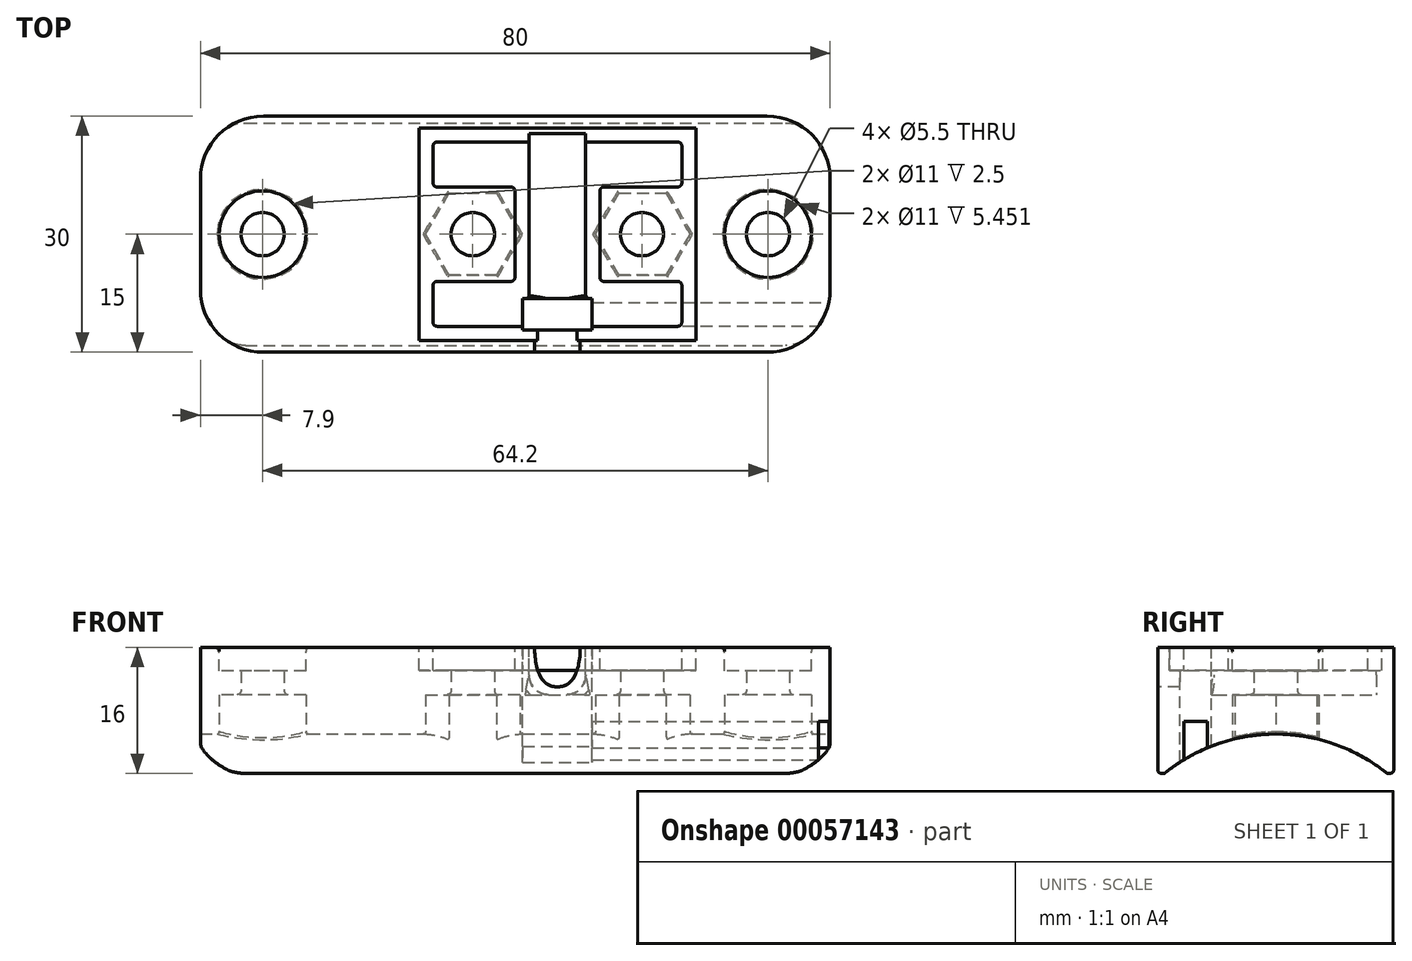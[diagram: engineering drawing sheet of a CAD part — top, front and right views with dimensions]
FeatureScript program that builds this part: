
annotation { "Feature Type Name" : "Feature", "Feature Type Description" : "" }
export const myFeature = defineFeature(function(context is Context, id is Id, definition is map)
    precondition{}
    {
        {
            var Q0;
            Q0=qCreatedBy(makeId("Top.planeOp"),FACE);
            var sketch = newSketch(context, id + "F0", { "sketchPlane" : qUnion([Q0])});
            skLineSegment(sketch, "E0.top", {"start": v(0, -15) * mm, "end": v(32, -15) * mm});
            skLineSegment(sketch, "E0.right", {"start": v(40, 7) * mm, "end": v(40, -7) * mm});
            skLineSegment(sketch, "E1", {"start": v(32, 15) * mm, "end": v(0, 15) * mm});
            skLineSegment(sketch, "E2.MirrorCS", {"start": v(0, -15) * mm, "end": v(-32, -15) * mm});
            skLineSegment(sketch, "E3.MirrorCS", {"start": v(-32, 15) * mm, "end": v(0, 15) * mm});
            skLineSegment(sketch, "E4.MirrorCS", {"start": v(-40, 7) * mm, "end": v(-40, -7) * mm});
            skCircle(sketch, "E5", {"center": v(-5.4, 0) * mm, "radius": 2.75 * mm});
            skCircle(sketch, "E6", {"center": v(16.1, 0) * mm, "radius": 2.75 * mm});
            skLineSegment(sketch, "E7", {"start": v(-5.4, 0) * mm, "end": v(16.1, 0) * mm, "construction": true});
            skLineSegment(sketch, "E8", {"start": v(16.1, 0) * mm, "end": v(40, 0) * mm, "construction": true});
            skLineSegment(sketch, "E9", {"start": v(0, 15) * mm, "end": v(0, -15) * mm, "construction": true});
            skLineSegment(sketch, "E10", {"start": v(-40, 0) * mm, "end": v(40, 0) * mm, "construction": true});
            skCircle(sketch, "E11", {"center": v(32.1, 0) * mm, "radius": 2.75 * mm});
            skCircle(sketch, "E12", {"center": v(-32.1, 0) * mm, "radius": 2.75 * mm});
            skLineSegment(sketch, "E13", {"start": v(-32.1, 0) * mm, "end": v(-40, 0) * mm, "construction": true});
            skLineSegment(sketch, "E14", {"start": v(-32.1, 0) * mm, "end": v(32.1, 0) * mm, "construction": true});
            skLineSegment(sketch, "E15", {"start": v(16.1, 0) * mm, "end": v(32.1, 0) * mm, "construction": true});
            skPoint(sketch, "E16.visualSharp", {"position": v(-40, 15) * mm});
            skArc(sketch, "E16.filletArc", {"start": v(-32, 15) * mm, "mid": v(-37.66, 12.66) * mm, "end": v(-40, 7) * mm});
            skPoint(sketch, "E17.visualSharp", {"position": v(-40, -15) * mm});
            skArc(sketch, "E17.filletArc", {"start": v(-40, -7) * mm, "mid": v(-37.66, -12.66) * mm, "end": v(-32, -15) * mm});
            skPoint(sketch, "E18.visualSharp", {"position": v(40, -15) * mm});
            skArc(sketch, "E18.filletArc", {"start": v(32, -15) * mm, "mid": v(37.66, -12.66) * mm, "end": v(40, -7) * mm});
            skPoint(sketch, "E19.visualSharp", {"position": v(40, 15) * mm});
            skArc(sketch, "E19.filletArc", {"start": v(40, 7) * mm, "mid": v(37.66, 12.66) * mm, "end": v(32, 15) * mm});
            skSolve(sketch);
        }
        {
            var Q0;
            Q0=makeQuery(id+"F0.imprint","IMPRINT",FACE,{"disambiguationData":[TD([[makeQuery(id+"F0.imprint","IMPRINT",EDGE,{"derivedFrom":sQuery(id+"F0.wireOp",EDGE,"E0.top")}),1.0]])]});
            extrude(context, id + "F1", {"entities" : qUnion([Q0]), "depth" : 14 * mm});
        }
        {
            var Q0;
            Q0=qCreatedBy(makeId("Right.planeOp"),FACE);
            var sketch = newSketch(context, id + "F2", { "sketchPlane" : qUnion([Q0])});
            skCircle(sketch, "E20", {"center": v(0, -17.5) * mm, "radius": 22.5 * mm});
            skSolve(sketch);
        }
        {
            var Q0;
            Q0=makeQuery(id+"F2.imprint","IMPRINT",FACE,{"disambiguationData":[TD([[makeQuery(id+"F2.imprint","IMPRINT",EDGE,{"derivedFrom":sQuery(id+"F2.wireOp",EDGE,"E20")}),1.0]])]});
            extrude(context, id + "F3", {"entities" : qUnion([Q0]), "operationType" : NewBodyOperationType.REMOVE, "oppositeDirection" : true, "depth" : 90 * mm, "symmetric" : true});
        }
        {
            var Q0;
            Q0=makeQuery(id+"F1.opExtrude","CAP_FACE",FACE,{"disambiguationData":[OSD([sQuery(id+"F0.wireOp",EDGE,"E0.top"),sQuery(id+"F0.wireOp",EDGE,"E0.right"),sQuery(id+"F0.wireOp",EDGE,"E1"),sQuery(id+"F0.wireOp",EDGE,"E2.MirrorCS"),sQuery(id+"F0.wireOp",EDGE,"E3.MirrorCS"),sQuery(id+"F0.wireOp",EDGE,"E4.MirrorCS"),sQuery(id+"F0.wireOp",EDGE,"E5"),sQuery(id+"F0.wireOp",EDGE,"E6"),sQuery(id+"F0.wireOp",EDGE,"E11"),sQuery(id+"F0.wireOp",EDGE,"E12")])],"isStart":false});
            var sketch = newSketch(context, id + "F4", { "sketchPlane" : qUnion([Q0])});
            skCircle(sketch, "E21", {"center": v(32.1, 0) * mm, "radius": 5.5 * mm});
            skCircle(sketch, "E22", {"center": v(-32.1, 0) * mm, "radius": 5.5 * mm});
            skSolve(sketch);
        }
        {
            var Q0;
            Q0=makeQuery(id+"F4.imprint","IMPRINT",FACE,{"disambiguationData":[TD([[makeQuery(id+"F4.imprint","IMPRINT",EDGE,{"derivedFrom":sQuery(id+"F4.wireOp",EDGE,"E21")}),1.0]])]});
            var Q1;
            Q1=makeQuery(id+"F4.imprint","IMPRINT",FACE,{"disambiguationData":[TD([[makeQuery(id+"F4.imprint","IMPRINT",EDGE,{"derivedFrom":sQuery(id+"F4.wireOp",EDGE,"E22")}),1.0]])]});
            var Q2;
            Q2=sQuery(id+"F4.wireOp",EDGE,"E21");
            var Q3;
            Q3=sQuery(id+"F4.wireOp",EDGE,"E22");
            extrude(context, id + "F5", {"entities" : qUnion([Q0, Q1]), "operationType" : NewBodyOperationType.REMOVE, "surfaceEntities" : qUnion([Q2, Q3]), "oppositeDirection" : true, "depth" : 1 * mm});
        }
        {
            var Q0;
            Q0=makeQuery(id+"F0.imprint","IMPRINT",FACE,{"disambiguationData":[TD([[makeQuery(id+"F0.imprint","IMPRINT",EDGE,{"derivedFrom":sQuery(id+"F0.wireOp",EDGE,"E0.top")}),1.0]])]});
            var sketch = newSketch(context, id + "F6", { "sketchPlane" : qUnion([Q0])});
            skCircle(sketch, "E23.cCircle", {"center": v(16.17, 0) * mm, "radius": 6 * mm, "construction": true});
            skLineSegment(sketch, "E23.0", {"start": v(13.17, 5.2) * mm, "end": v(19.17, 5.2) * mm});
            skLineSegment(sketch, "E23.1", {"start": v(19.17, 5.2) * mm, "end": v(22.17, 0) * mm});
            skLineSegment(sketch, "E23.2", {"start": v(22.17, 0) * mm, "end": v(19.17, -5.2) * mm});
            skLineSegment(sketch, "E23.3", {"start": v(19.17, -5.2) * mm, "end": v(13.17, -5.2) * mm});
            skLineSegment(sketch, "E23.4", {"start": v(13.17, -5.2) * mm, "end": v(10.17, 0) * mm});
            skLineSegment(sketch, "E23.5", {"start": v(10.17, 0) * mm, "end": v(13.17, 5.2) * mm});
            skCircle(sketch, "E24.cCircle", {"center": v(-5.4, 0) * mm, "radius": 6 * mm, "construction": true});
            skLineSegment(sketch, "E24.3", {"start": v(-2.4, -5.2) * mm, "end": v(-8.4, -5.2) * mm});
            skLineSegment(sketch, "E24.5", {"start": v(-11.4, 0) * mm, "end": v(-8.4, 5.2) * mm});
            skLineSegment(sketch, "E24.0", {"start": v(-8.4, 5.2) * mm, "end": v(-2.4, 5.2) * mm});
            skLineSegment(sketch, "E24.1", {"start": v(-2.4, 5.2) * mm, "end": v(0.6, 0) * mm});
            skLineSegment(sketch, "E24.2", {"start": v(0.6, 0) * mm, "end": v(-2.4, -5.2) * mm});
            skLineSegment(sketch, "E24.4", {"start": v(-8.4, -5.2) * mm, "end": v(-11.4, 0) * mm});
            skCircle(sketch, "E25", {"center": v(-32.1, 0) * mm, "radius": 5.5 * mm});
            skCircle(sketch, "E26", {"center": v(32.1, 0) * mm, "radius": 5.5 * mm});
            skLineSegment(sketch, "E27", {"start": v(-11.4, 0) * mm, "end": v(22.17, 0) * mm, "construction": true});
            skSolve(sketch);
        }
        {
            var Q0;
            Q0=qSketchRegion(id+"F6",true);
            extrude(context, id + "F7", {"entities" : qUnion([Q0]), "operationType" : NewBodyOperationType.REMOVE, "depth" : 10 * mm});
        }
        {
            var Q0;
            Q0=makeQuery(id+"F1.opExtrude","CAP_FACE",FACE,{"disambiguationData":[OSD([sQuery(id+"F0.wireOp",EDGE,"E0.top"),sQuery(id+"F0.wireOp",EDGE,"E0.right"),sQuery(id+"F0.wireOp",EDGE,"E1"),sQuery(id+"F0.wireOp",EDGE,"E2.MirrorCS"),sQuery(id+"F0.wireOp",EDGE,"E3.MirrorCS"),sQuery(id+"F0.wireOp",EDGE,"E4.MirrorCS"),sQuery(id+"F0.wireOp",EDGE,"E5"),sQuery(id+"F0.wireOp",EDGE,"E6"),sQuery(id+"F0.wireOp",EDGE,"E11"),sQuery(id+"F0.wireOp",EDGE,"E12")])],"isStart":false});
            var sketch = newSketch(context, id + "F8", { "sketchPlane" : qUnion([Q0])});
            skLineSegment(sketch, "E28", {"start": v(5.35, 15) * mm, "end": v(5.35, -15) * mm, "construction": true});
            skLineSegment(sketch, "E29", {"start": v(-2.65, 0) * mm, "end": v(13.35, 0) * mm, "construction": true});
            skPoint(sketch, "E30", {"position": v(5.35, 0) * mm});
            skLineSegment(sketch, "E31.bottom", {"start": v(1.75, -12.2) * mm, "end": v(8.95, -12.2) * mm});
            skLineSegment(sketch, "E31.top", {"start": v(1.75, 12.8) * mm, "end": v(8.95, 12.8) * mm});
            skLineSegment(sketch, "E31.left", {"start": v(1.75, -12.2) * mm, "end": v(1.75, 12.8) * mm});
            skLineSegment(sketch, "E31.right", {"start": v(8.95, -12.2) * mm, "end": v(8.95, 12.8) * mm});
            skPoint(sketch, "E32", {"position": v(5.35, -12.2) * mm});
            skLineSegment(sketch, "E33.bottom", {"start": v(2.55, -15) * mm, "end": v(8.15, -15) * mm});
            skLineSegment(sketch, "E33.top", {"start": v(2.55, -12.2) * mm, "end": v(8.15, -12.2) * mm});
            skLineSegment(sketch, "E33.left", {"start": v(2.55, -15) * mm, "end": v(2.55, -12.2) * mm});
            skLineSegment(sketch, "E33.right", {"start": v(8.15, -15) * mm, "end": v(8.15, -12.2) * mm});
            skLineSegment(sketch, "E34.bottom", {"start": v(0.95, -12.2) * mm, "end": v(9.75, -12.2) * mm});
            skLineSegment(sketch, "E34.top", {"start": v(0.95, -8.2) * mm, "end": v(9.75, -8.2) * mm});
            skLineSegment(sketch, "E34.left", {"start": v(0.95, -12.2) * mm, "end": v(0.95, -8.2) * mm});
            skLineSegment(sketch, "E34.right", {"start": v(9.75, -12.2) * mm, "end": v(9.75, -8.2) * mm});
            skSolve(sketch);
        }
        {
            var Q0;
            {var subQ5=sQuery(id+"F8.wireOp",EDGE,"E31.top");Q0=makeQuery(id+"F8.imprint","IMPRINT",FACE,{"disambiguationData":[TD([[makeQuery(id+"F8.imprint","IMPRINT",EDGE,{"derivedFrom":subQ5}),-1.0]])]});}
            var Q1;
            {var subQ0=sQuery(id+"F8.wireOp",EDGE,"E34.left");Q1=makeQuery(id+"F8.imprint","IMPRINT",FACE,{"disambiguationData":[TD([[makeQuery(id+"F8.imprint","IMPRINT",EDGE,{"derivedFrom":subQ0}),-1.0]])]});}
            var Q2;
            {var subQ3=sQuery(id+"F8.wireOp",EDGE,"E31.left");var subQ5=sQuery(id+"F8.wireOp",EDGE,"E34.bottom");var subQ9=makeQuery(id+"F8.imprint","INTERSECT",VERTEX,{"derivedFrom":[subQ3,subQ5]});Q2=makeQuery(id+"F8.imprint","IMPRINT",FACE,{"disambiguationData":[TD([[makeQuery(id+"F8.imprint","IMPRINT",EDGE,{"disambiguationData":[TD([[subQ9,-1.0]])],"derivedFrom":subQ3}),-1.0]])]});}
            var Q3;
            {var subQ0=sQuery(id+"F8.wireOp",EDGE,"E34.right");Q3=makeQuery(id+"F8.imprint","IMPRINT",FACE,{"disambiguationData":[TD([[makeQuery(id+"F8.imprint","IMPRINT",EDGE,{"derivedFrom":subQ0}),1.0]])]});}
            extrude(context, id + "F9", {"entities" : qUnion([Q0, Q1, Q2, Q3]), "operationType" : NewBodyOperationType.REMOVE, "oppositeDirection" : true, "depth" : 4 * mm});
        }
        {
            var Q0;
            Q0=makeQuery(id+"F1.opExtrude","CAP_FACE",FACE,{"disambiguationData":[OSD([sQuery(id+"F0.wireOp",EDGE,"E0.top"),sQuery(id+"F0.wireOp",EDGE,"E0.right"),sQuery(id+"F0.wireOp",EDGE,"E1"),sQuery(id+"F0.wireOp",EDGE,"E2.MirrorCS"),sQuery(id+"F0.wireOp",EDGE,"E3.MirrorCS"),sQuery(id+"F0.wireOp",EDGE,"E4.MirrorCS"),sQuery(id+"F0.wireOp",EDGE,"E5"),sQuery(id+"F0.wireOp",EDGE,"E6"),sQuery(id+"F0.wireOp",EDGE,"E11"),sQuery(id+"F0.wireOp",EDGE,"E12")])],"isStart":false});
            var sketch = newSketch(context, id + "F10", { "sketchPlane" : qUnion([Q0])});
            skLineSegment(sketch, "E35", {"start": v(2.55, -15) * mm, "end": v(-13.65, -15) * mm});
            skLineSegment(sketch, "E36", {"start": v(-13.65, -15) * mm, "end": v(-13.65, 15) * mm});
            skLineSegment(sketch, "E37", {"start": v(-13.65, 15) * mm, "end": v(24.35, 15) * mm});
            skLineSegment(sketch, "E38", {"start": v(24.35, 15) * mm, "end": v(24.35, -15) * mm});
            skLineSegment(sketch, "E39", {"start": v(24.35, -15) * mm, "end": v(8.15, -15) * mm});
            skLineSegment(sketch, "E40", {"start": v(2.55, -15) * mm, "end": v(8.15, -15) * mm, "construction": true});
            skSolve(sketch);
        }
        {
            var Q0;
            {var subQ0=sQuery(id+"F0.wireOp",EDGE,"E0.top");var subQ1=sQuery(id+"F0.wireOp",EDGE,"E1");var subQ2=sQuery(id+"F0.wireOp",EDGE,"E2.MirrorCS");var subQ3=sQuery(id+"F0.wireOp",EDGE,"E3.MirrorCS");var subQ4=sQuery(id+"F0.wireOp",EDGE,"E4.MirrorCS");Q0=makeQuery(id+"F0dNFgO26YUrEqA_1.boolean.opBoolean","SPLIT",FACE,{"disambiguationData":[TD([makeQuery(id+"F1.opExtrude","SWEPT_FACE",FACE,{"disambiguationData":[OSD([subQ4])]})])],"derivedFrom":makeQuery(id+"F1.opExtrude","CAP_FACE",FACE,{"disambiguationData":[OSD([subQ0,sQuery(id+"F0.wireOp",EDGE,"E0.right"),subQ1,subQ2,subQ3,subQ4,sQuery(id+"F0.wireOp",EDGE,"E5"),sQuery(id+"F0.wireOp",EDGE,"E6"),sQuery(id+"F0.wireOp",EDGE,"E11"),sQuery(id+"F0.wireOp",EDGE,"E12")])],"isStart":false})});}
            var Q1;
            {var subQ0=sQuery(id+"F0.wireOp",EDGE,"E0.top");var subQ1=sQuery(id+"F0.wireOp",EDGE,"E0.right");var subQ2=sQuery(id+"F0.wireOp",EDGE,"E1");var subQ3=sQuery(id+"F0.wireOp",EDGE,"E2.MirrorCS");var subQ4=sQuery(id+"F0.wireOp",EDGE,"E3.MirrorCS");Q1=makeQuery(id+"F0dNFgO26YUrEqA_1.boolean.opBoolean","SPLIT",FACE,{"disambiguationData":[TD([makeQuery(id+"F1.opExtrude","SWEPT_FACE",FACE,{"disambiguationData":[OSD([subQ1])]})])],"derivedFrom":makeQuery(id+"F1.opExtrude","CAP_FACE",FACE,{"disambiguationData":[OSD([subQ0,subQ1,subQ2,subQ3,subQ4,sQuery(id+"F0.wireOp",EDGE,"E4.MirrorCS"),sQuery(id+"F0.wireOp",EDGE,"E5"),sQuery(id+"F0.wireOp",EDGE,"E6"),sQuery(id+"F0.wireOp",EDGE,"E11"),sQuery(id+"F0.wireOp",EDGE,"E12")])],"isStart":false})});}
            extrude(context, id + "F11", {"entities" : qUnion([Q0, Q1]), "operationType" : NewBodyOperationType.ADD, "depth" : 2 * mm});
        }
        {
            var Q0;
            Q0=makeQuery(id+"F9.boolean.opBoolean","COPY",FACE,{"derivedFrom":makeQuery(id+"F9.opExtrude","CAP_FACE",FACE,{"disambiguationData":[OSD([sQuery(id+"F8.wireOp",EDGE,"E31.top"),sQuery(id+"F8.wireOp",EDGE,"E31.left"),sQuery(id+"F8.wireOp",EDGE,"E31.right"),sQuery(id+"F8.wireOp",EDGE,"E34.bottom"),sQuery(id+"F8.wireOp",EDGE,"E34.top"),sQuery(id+"F8.wireOp",EDGE,"E34.left"),sQuery(id+"F8.wireOp",EDGE,"E34.right")])],"isStart":false})});
            var sketch = newSketch(context, id + "F12", { "sketchPlane" : qUnion([Q0])});
            skLineSegment(sketch, "E41", {"start": v(5.35, -9.7) * mm, "end": v(5.35, 12.8) * mm, "construction": true});
            skSolve(sketch);
        }
        {
            var Q0;
            {var subQ0=sQuery(id+"F8.wireOp",EDGE,"E34.top");var subQ1=sQuery(id+"F8.wireOp",EDGE,"E31.left");Q0=makeQuery(id+"F11.boolean.opBoolean","MERGE",EDGE,{"derivedFrom":[makeQuery(id+"F9.boolean.opBoolean","COPY",EDGE,{"derivedFrom":makeQuery(id+"F9.opExtrude","SWEPT_EDGE",EDGE,{"disambiguationData":[OSD([subQ1,subQ0])]})}),makeQuery(id+"F11.opExtrude","SWEPT_EDGE",EDGE,{"disambiguationData":[OSD([subQ1,subQ0])]})]});}
            var Q1;
            {var subQ0=sQuery(id+"F8.wireOp",EDGE,"E34.top");var subQ1=sQuery(id+"F8.wireOp",EDGE,"E31.right");Q1=makeQuery(id+"F11.boolean.opBoolean","MERGE",EDGE,{"derivedFrom":[makeQuery(id+"F9.boolean.opBoolean","COPY",EDGE,{"derivedFrom":makeQuery(id+"F9.opExtrude","SWEPT_EDGE",EDGE,{"disambiguationData":[OSD([subQ1,subQ0])]})}),makeQuery(id+"F11.opExtrude","SWEPT_EDGE",EDGE,{"disambiguationData":[OSD([subQ1,subQ0])]})]});}
            var Q2;
            Q2=makeQuery(id+"F11.opExtrude","CAP_EDGE",EDGE,{"disambiguationData":[OSD([sQuery(id+"F4.wireOp",EDGE,"E21")])],"isStart":false});
            var Q3;
            Q3=makeQuery(id+"F11.opExtrude","CAP_EDGE",EDGE,{"disambiguationData":[OSD([sQuery(id+"F4.wireOp",EDGE,"E22")])],"isStart":false});
            var Q4;
            Q4=makeQuery(id+"F5.boolean.opBoolean","COPY",EDGE,{"derivedFrom":makeQuery(id+"F5.opExtrude","CAP_EDGE",EDGE,{"disambiguationData":[OSD([sQuery(id+"F0.wireOp",EDGE,"E12")])],"isStart":false})});
            var Q5;
            Q5=makeQuery(id+"F5.boolean.opBoolean","COPY",EDGE,{"derivedFrom":makeQuery(id+"F5.opExtrude","CAP_EDGE",EDGE,{"disambiguationData":[OSD([sQuery(id+"F0.wireOp",EDGE,"E11")])],"isStart":false})});
            var Q6;
            Q6=makeQuery(id+"F7.boolean.opBoolean","INTERSECT",EDGE,{"derivedFrom":[makeQuery(id+"F1.opExtrude","SWEPT_FACE",FACE,{"disambiguationData":[OSD([sQuery(id+"F0.wireOp",EDGE,"E12")])]}),makeQuery(id+"F7.opExtrude","CAP_FACE",FACE,{"disambiguationData":[OSD([sQuery(id+"F6.wireOp",EDGE,"E25")])],"isStart":false})]});
            var Q7;
            Q7=makeQuery(id+"F7.boolean.opBoolean","INTERSECT",EDGE,{"derivedFrom":[makeQuery(id+"F1.opExtrude","SWEPT_FACE",FACE,{"disambiguationData":[OSD([sQuery(id+"F0.wireOp",EDGE,"E5")])]}),makeQuery(id+"F7.opExtrude","CAP_FACE",FACE,{"disambiguationData":[OSD([sQuery(id+"F6.wireOp",EDGE,"E24.3"),sQuery(id+"F6.wireOp",EDGE,"E24.5"),sQuery(id+"F6.wireOp",EDGE,"E24.0"),sQuery(id+"F6.wireOp",EDGE,"E24.1"),sQuery(id+"F6.wireOp",EDGE,"E24.2"),sQuery(id+"F6.wireOp",EDGE,"E24.4")])],"isStart":false})]});
            var Q8;
            Q8=makeQuery(id+"F7.boolean.opBoolean","INTERSECT",EDGE,{"derivedFrom":[makeQuery(id+"F1.opExtrude","SWEPT_FACE",FACE,{"disambiguationData":[OSD([sQuery(id+"F0.wireOp",EDGE,"E6")])]}),makeQuery(id+"F7.opExtrude","CAP_FACE",FACE,{"disambiguationData":[OSD([sQuery(id+"F6.wireOp",EDGE,"E23.0"),sQuery(id+"F6.wireOp",EDGE,"E23.1"),sQuery(id+"F6.wireOp",EDGE,"E23.2"),sQuery(id+"F6.wireOp",EDGE,"E23.3"),sQuery(id+"F6.wireOp",EDGE,"E23.4"),sQuery(id+"F6.wireOp",EDGE,"E23.5")])],"isStart":false})]});
            var Q9;
            Q9=makeQuery(id+"F7.boolean.opBoolean","INTERSECT",EDGE,{"derivedFrom":[makeQuery(id+"F1.opExtrude","SWEPT_FACE",FACE,{"disambiguationData":[OSD([sQuery(id+"F0.wireOp",EDGE,"E11")])]}),makeQuery(id+"F7.opExtrude","CAP_FACE",FACE,{"disambiguationData":[OSD([sQuery(id+"F6.wireOp",EDGE,"E26")])],"isStart":false})]});
            var Q10;
            Q10=makeQuery(id+"F1.opExtrude","CAP_EDGE",EDGE,{"disambiguationData":[OSD([sQuery(id+"F0.wireOp",EDGE,"E1"),sQuery(id+"F0.wireOp",EDGE,"E3.MirrorCS")])],"isStart":true});
            var Q11;
            Q11=makeQuery(id+"F1.opExtrude","CAP_EDGE",EDGE,{"disambiguationData":[OSD([sQuery(id+"F0.wireOp",EDGE,"E0.top"),sQuery(id+"F0.wireOp",EDGE,"E2.MirrorCS")])],"isStart":true});
            fillet(context, id + "F13", {"entities" : qUnion([Q0, Q1, Q2, Q3, Q4, Q5, Q6, Q7, Q8, Q9, Q10, Q11]), "radius" : 0.5 * mm, "tangentPropagation" : true, "allowEdgeOverflow" : false});
        }
        {
            var Q0;
            {var subQ0=sQuery(id+"F0.wireOp",EDGE,"E0.top");var subQ1=sQuery(id+"F0.wireOp",EDGE,"E2.MirrorCS");Q0=makeQuery(id+"F11.boolean.opBoolean","MERGE",FACE,{"derivedFrom":[makeQuery(id+"F1.opExtrude","SWEPT_FACE",FACE,{"disambiguationData":[OSD([subQ0,subQ1])]}),makeQuery(id+"F11.opExtrude","SWEPT_FACE",FACE,{"disambiguationData":[OSD([subQ0,subQ1])]})]});}
            var sketch = newSketch(context, id + "F14", { "sketchPlane" : qUnion([Q0])});
            skLineSegment(sketch, "E42", {"start": v(5.35, 14) * mm, "end": v(5.35, 16) * mm, "construction": true});
            skLineSegment(sketch, "E43", {"start": v(5.35, 16) * mm, "end": v(5.35, 0) * mm, "construction": true});
            skLineSegment(sketch, "E44", {"start": v(5.35, 16) * mm, "end": v(2.45, 16) * mm});
            skLineSegment(sketch, "E45.MirrorCS", {"start": v(5.35, 16) * mm, "end": v(5.35, 32) * mm});
            skLineSegment(sketch, "E46.MirrorCS", {"start": v(5.35, 16) * mm, "end": v(8.25, 16) * mm});
            skPoint(sketch, "E47", {"position": v(5.35, 11) * mm});
            skFitSpline(sketch, "E48", {"points": [v(2.45, 16) * mm, v(5.35, 11) * mm], "startDerivative": vector(0.04, -6.55) * mm, "endDerivative": vector(7.15, 0.03) * mm});
            skFitSpline(sketch, "E49.MirrorCS", {"points": [v(8.25, 16) * mm, v(5.35, 11) * mm], "startDerivative": vector(-0.04, -6.55) * mm, "endDerivative": vector(-7.15, 0.03) * mm});
            skSolve(sketch);
        }
        {
            var Q0;
            Q0=makeQuery(id+"F14.imprint","IMPRINT",FACE,{"disambiguationData":[TD([[makeQuery(id+"F14.imprint","IMPRINT",EDGE,{"derivedFrom":sQuery(id+"F14.wireOp",EDGE,"E44")}),1.0]])]});
            extrude(context, id + "F15", {"entities" : qUnion([Q0]), "operationType" : NewBodyOperationType.REMOVE, "endBound" : BoundingType.UP_TO_NEXT, "oppositeDirection" : true, "depth" : 25 * mm});
        }
        {
            var Q0;
            {var subQ3=sQuery(id+"F8.wireOp",EDGE,"E31.left");var subQ5=sQuery(id+"F8.wireOp",EDGE,"E34.bottom");var subQ9=makeQuery(id+"F8.imprint","INTERSECT",VERTEX,{"derivedFrom":[subQ3,subQ5]});Q0=makeQuery(id+"F8.imprint","IMPRINT",FACE,{"disambiguationData":[TD([[makeQuery(id+"F8.imprint","IMPRINT",EDGE,{"disambiguationData":[TD([[subQ9,-1.0]])],"derivedFrom":subQ3}),-1.0]])]});}
            var Q1;
            {var subQ0=sQuery(id+"F8.wireOp",EDGE,"E34.left");Q1=makeQuery(id+"F8.imprint","IMPRINT",FACE,{"disambiguationData":[TD([[makeQuery(id+"F8.imprint","IMPRINT",EDGE,{"derivedFrom":subQ0}),-1.0]])]});}
            var Q2;
            {var subQ0=sQuery(id+"F8.wireOp",EDGE,"E34.right");Q2=makeQuery(id+"F8.imprint","IMPRINT",FACE,{"disambiguationData":[TD([[makeQuery(id+"F8.imprint","IMPRINT",EDGE,{"derivedFrom":subQ0}),1.0]])]});}
            extrude(context, id + "F16", {"entities" : qUnion([Q0, Q1, Q2]), "operationType" : NewBodyOperationType.REMOVE, "endBound" : BoundingType.THROUGH_ALL, "oppositeDirection" : true, "depth" : 5.5 * mm});
        }
        {
            var Q0;
            {var subQ0=sQuery(id+"F0.wireOp",EDGE,"E0.right");Q0=makeQuery(id+"F11.boolean.opBoolean","MERGE",FACE,{"derivedFrom":[makeQuery(id+"F1.opExtrude","SWEPT_FACE",FACE,{"disambiguationData":[OSD([subQ0])]}),makeQuery(id+"F11.opExtrude","SWEPT_FACE",FACE,{"disambiguationData":[OSD([subQ0])]})]});}
            var sketch = newSketch(context, id + "F17", { "sketchPlane" : qUnion([Q0])});
            skLineSegment(sketch, "E50", {"start": v(0, 0) * mm, "end": v(0, 16) * mm, "construction": true});
            skLineSegment(sketch, "E51.MirrorCS", {"start": v(-8.68, 6.57) * mm, "end": v(-8.68, 0) * mm});
            skLineSegment(sketch, "E52.MirrorCS", {"start": v(-11.68, 3.88) * mm, "end": v(-11.68, 6.57) * mm});
            skLineSegment(sketch, "E53.MirrorCS", {"start": v(-11.68, 6.57) * mm, "end": v(-8.68, 6.57) * mm});
            skLineSegment(sketch, "E54", {"start": v(-11.68, 3.88) * mm, "end": v(-11.68, 0) * mm});
            skLineSegment(sketch, "E55", {"start": v(-11.68, 0) * mm, "end": v(-8.68, 0) * mm});
            skSolve(sketch);
        }
        {
            var Q0;
            {var subQ5=sQuery(id+"F17.wireOp",EDGE,"70751b96-99b8-413a-8478-21d8ff6998ed");Q0=makeQuery(id+"F17.imprint","IMPRINT",FACE,{"disambiguationData":[TD([[makeQuery(id+"F17.imprint","IMPRINT",EDGE,{"derivedFrom":subQ5}),1.0]])]});}
            var Q1;
            {var subQ0=sQuery(id+"F17.wireOp",EDGE,"E53.MirrorCS");Q1=makeQuery(id+"F17.imprint","IMPRINT",FACE,{"disambiguationData":[TD([[makeQuery(id+"F17.imprint","IMPRINT",EDGE,{"derivedFrom":subQ0}),-1.0]])]});}
            extrude(context, id + "F18", {"entities" : qUnion([Q0, Q1]), "operationType" : NewBodyOperationType.REMOVE, "oppositeDirection" : true, "depth" : 34.5 * mm});
        }
        {
            var Q0;
            Q0=makeQuery(id+"F9.boolean.opBoolean","COPY",EDGE,{"derivedFrom":makeQuery(id+"F9.opExtrude","CAP_EDGE",EDGE,{"disambiguationData":[OSD([sQuery(id+"F8.wireOp",EDGE,"E31.right")])],"isStart":false})});
            var Q1;
            Q1=makeQuery(id+"F9.boolean.opBoolean","COPY",EDGE,{"derivedFrom":makeQuery(id+"F9.opExtrude","CAP_EDGE",EDGE,{"disambiguationData":[OSD([sQuery(id+"F8.wireOp",EDGE,"E31.left")])],"isStart":false})});
            fillet(context, id + "F19", {"entities" : qUnion([Q0, Q1]), "radius" : 2.5 * mm, "tangentPropagation" : true, "allowEdgeOverflow" : false});
        }
        {
            var Q0;
            Q0=makeQuery(id+"F11.opExtrude","CAP_FACE",FACE,{"disambiguationData":[OSD([sQuery(id+"F0.wireOp",EDGE,"E0.top"),sQuery(id+"F0.wireOp",EDGE,"E0.right"),sQuery(id+"F0.wireOp",EDGE,"E1"),sQuery(id+"F0.wireOp",EDGE,"E2.MirrorCS"),sQuery(id+"F0.wireOp",EDGE,"E3.MirrorCS"),sQuery(id+"F0.wireOp",EDGE,"E4.MirrorCS"),sQuery(id+"F0.wireOp",EDGE,"E5"),sQuery(id+"F0.wireOp",EDGE,"E6"),sQuery(id+"F0.wireOp",EDGE,"E11"),sQuery(id+"F0.wireOp",EDGE,"E12")])],"isStart":false});
            var sketch = newSketch(context, id + "F20", { "sketchPlane" : qUnion([Q0])});
            skLineSegment(sketch, "E56", {"start": v(-12.25, 13.5) * mm, "end": v(5.35, 13.5) * mm});
            skLineSegment(sketch, "E57", {"start": v(5.35, 13.5) * mm, "end": v(5.35, 11.7) * mm});
            skLineSegment(sketch, "E58", {"start": v(-10.45, 6) * mm, "end": v(-0.05, 6) * mm});
            skLineSegment(sketch, "E59", {"start": v(-0.05, 6) * mm, "end": v(-0.05, -6) * mm});
            skLineSegment(sketch, "E60", {"start": v(-0.05, -6) * mm, "end": v(-10.45, -6) * mm});
            skLineSegment(sketch, "E61", {"start": v(-10.45, -6) * mm, "end": v(-10.45, -11.7) * mm});
            skLineSegment(sketch, "E62", {"start": v(-10.45, -11.7) * mm, "end": v(5.35, -11.7) * mm});
            skLineSegment(sketch, "E63", {"start": v(5.35, -11.7) * mm, "end": v(5.35, -13.5) * mm});
            skLineSegment(sketch, "E64", {"start": v(5.35, -13.5) * mm, "end": v(-12.25, -13.5) * mm});
            skLineSegment(sketch, "E65", {"start": v(-12.25, -13.5) * mm, "end": v(-12.25, 13.5) * mm});
            skLineSegment(sketch, "E66", {"start": v(5.35, 11.7) * mm, "end": v(-10.45, 11.7) * mm});
            skLineSegment(sketch, "E67", {"start": v(-10.45, 11.7) * mm, "end": v(-10.45, 6) * mm});
            skLineSegment(sketch, "E68", {"start": v(-13.64, 0) * mm, "end": v(0, 0) * mm, "construction": true});
            skPoint(sketch, "E69", {"position": v(-0.05, 0) * mm});
            skLineSegment(sketch, "E70.MirrorCS", {"start": v(22.95, -13.5) * mm, "end": v(22.95, 13.5) * mm});
            skLineSegment(sketch, "E71.MirrorCS", {"start": v(22.95, 13.5) * mm, "end": v(5.35, 13.5) * mm});
            skLineSegment(sketch, "E72.MirrorCS", {"start": v(5.35, 11.7) * mm, "end": v(21.15, 11.7) * mm});
            skLineSegment(sketch, "E73.MirrorCS", {"start": v(21.15, 11.7) * mm, "end": v(21.15, 6) * mm});
            skLineSegment(sketch, "E74.MirrorCS", {"start": v(21.15, 6) * mm, "end": v(10.75, 6) * mm});
            skLineSegment(sketch, "E75.MirrorCS", {"start": v(10.75, 6) * mm, "end": v(10.75, -6) * mm});
            skLineSegment(sketch, "E76.MirrorCS", {"start": v(10.75, -6) * mm, "end": v(21.15, -6) * mm});
            skLineSegment(sketch, "E77.MirrorCS", {"start": v(21.15, -6) * mm, "end": v(21.15, -11.7) * mm});
            skLineSegment(sketch, "E78.MirrorCS", {"start": v(5.35, -13.5) * mm, "end": v(22.95, -13.5) * mm});
            skLineSegment(sketch, "E79.MirrorCS", {"start": v(21.15, -11.7) * mm, "end": v(5.35, -11.7) * mm});
            skSolve(sketch);
        }
        {
            var Q0;
            {var subQ25=sQuery(id+"F20.wireOp",EDGE,"E56");Q0=makeQuery(id+"F20.imprint","IMPRINT",FACE,{"disambiguationData":[TD([[makeQuery(id+"F20.imprint","IMPRINT",EDGE,{"derivedFrom":subQ25}),-1.0]])]});}
            var Q1;
            {var subQ18=sQuery(id+"F20.wireOp",EDGE,"E70.MirrorCS");Q1=makeQuery(id+"F20.imprint","IMPRINT",FACE,{"disambiguationData":[TD([[makeQuery(id+"F20.imprint","IMPRINT",EDGE,{"derivedFrom":subQ18}),1.0]])]});}
            var Q2;
            {var subQ12=sQuery(id+"F20.wireOp",EDGE,"E63");Q2=makeQuery(id+"F20.imprint","IMPRINT",FACE,{"disambiguationData":[TD([[makeQuery(id+"F20.imprint","IMPRINT",EDGE,{"derivedFrom":subQ12}),-1.0]])]});}
            var Q3;
            {var subQ9=sQuery(id+"F20.wireOp",EDGE,"E63");Q3=makeQuery(id+"F20.imprint","IMPRINT",FACE,{"disambiguationData":[TD([[makeQuery(id+"F20.imprint","IMPRINT",EDGE,{"derivedFrom":subQ9}),1.0]])]});}
            extrude(context, id + "F21", {"entities" : qUnion([Q0, Q1, Q2, Q3]), "operationType" : NewBodyOperationType.REMOVE, "oppositeDirection" : true, "depth" : 2.9 * mm});
        }
        {
            var Q0;
            Q0=makeQuery(id+"F21.boolean.opBoolean","COPY",EDGE,{"derivedFrom":makeQuery(id+"F21.opExtrude","SWEPT_EDGE",EDGE,{"disambiguationData":[OSD([sQuery(id+"F20.wireOp",EDGE,"E58"),sQuery(id+"F20.wireOp",EDGE,"E59")])]})});
            var Q1;
            Q1=makeQuery(id+"F21.boolean.opBoolean","COPY",EDGE,{"derivedFrom":makeQuery(id+"F21.opExtrude","SWEPT_EDGE",EDGE,{"disambiguationData":[OSD([sQuery(id+"F20.wireOp",EDGE,"E58"),sQuery(id+"F20.wireOp",EDGE,"E67")])]})});
            var Q2;
            Q2=makeQuery(id+"F21.boolean.opBoolean","COPY",EDGE,{"derivedFrom":makeQuery(id+"F21.opExtrude","SWEPT_EDGE",EDGE,{"disambiguationData":[OSD([sQuery(id+"F20.wireOp",EDGE,"E66"),sQuery(id+"F20.wireOp",EDGE,"E67")])]})});
            var Q3;
            Q3=makeQuery(id+"F21.boolean.opBoolean","COPY",EDGE,{"derivedFrom":makeQuery(id+"F21.opExtrude","SWEPT_EDGE",EDGE,{"disambiguationData":[OSD([sQuery(id+"F20.wireOp",EDGE,"E73.MirrorCS"),sQuery(id+"F20.wireOp",EDGE,"E74.MirrorCS")])]})});
            var Q4;
            Q4=makeQuery(id+"F21.boolean.opBoolean","COPY",EDGE,{"derivedFrom":makeQuery(id+"F21.opExtrude","SWEPT_EDGE",EDGE,{"disambiguationData":[OSD([sQuery(id+"F20.wireOp",EDGE,"E60"),sQuery(id+"F20.wireOp",EDGE,"E61")])]})});
            var Q5;
            Q5=makeQuery(id+"F21.boolean.opBoolean","COPY",EDGE,{"derivedFrom":makeQuery(id+"F21.opExtrude","SWEPT_EDGE",EDGE,{"disambiguationData":[OSD([sQuery(id+"F20.wireOp",EDGE,"E61"),sQuery(id+"F20.wireOp",EDGE,"E62")])]})});
            var Q6;
            Q6=makeQuery(id+"F21.boolean.opBoolean","COPY",EDGE,{"derivedFrom":makeQuery(id+"F21.opExtrude","SWEPT_EDGE",EDGE,{"disambiguationData":[OSD([sQuery(id+"F20.wireOp",EDGE,"E77.MirrorCS"),sQuery(id+"F20.wireOp",EDGE,"E79.MirrorCS")])]})});
            var Q7;
            Q7=makeQuery(id+"F21.boolean.opBoolean","COPY",EDGE,{"derivedFrom":makeQuery(id+"F21.opExtrude","SWEPT_EDGE",EDGE,{"disambiguationData":[OSD([sQuery(id+"F20.wireOp",EDGE,"E59"),sQuery(id+"F20.wireOp",EDGE,"E60")])]})});
            var Q8;
            Q8=makeQuery(id+"F21.boolean.opBoolean","COPY",EDGE,{"derivedFrom":makeQuery(id+"F21.opExtrude","SWEPT_EDGE",EDGE,{"disambiguationData":[OSD([sQuery(id+"F20.wireOp",EDGE,"E75.MirrorCS"),sQuery(id+"F20.wireOp",EDGE,"E76.MirrorCS")])]})});
            var Q9;
            Q9=makeQuery(id+"F21.boolean.opBoolean","COPY",EDGE,{"derivedFrom":makeQuery(id+"F21.opExtrude","SWEPT_EDGE",EDGE,{"disambiguationData":[OSD([sQuery(id+"F20.wireOp",EDGE,"E76.MirrorCS"),sQuery(id+"F20.wireOp",EDGE,"E77.MirrorCS")])]})});
            var Q10;
            Q10=makeQuery(id+"F21.boolean.opBoolean","COPY",EDGE,{"derivedFrom":makeQuery(id+"F21.opExtrude","SWEPT_EDGE",EDGE,{"disambiguationData":[OSD([sQuery(id+"F20.wireOp",EDGE,"E74.MirrorCS"),sQuery(id+"F20.wireOp",EDGE,"E75.MirrorCS")])]})});
            var Q11;
            Q11=makeQuery(id+"F21.boolean.opBoolean","COPY",EDGE,{"derivedFrom":makeQuery(id+"F21.opExtrude","SWEPT_EDGE",EDGE,{"disambiguationData":[OSD([sQuery(id+"F20.wireOp",EDGE,"E72.MirrorCS"),sQuery(id+"F20.wireOp",EDGE,"E73.MirrorCS")])]})});
            fillet(context, id + "F22", {"entities" : qUnion([Q0, Q1, Q2, Q3, Q4, Q5, Q6, Q7, Q8, Q9, Q10, Q11]), "radius" : 0.5 * mm, "tangentPropagation" : true, "allowEdgeOverflow" : false});
        }
        {
            var Q0;
            {var subQ0=makeQuery(id+"F3.boolean.opBoolean","COPY",FACE,{"derivedFrom":makeQuery(id+"F3.opExtrude","SWEPT_FACE",FACE,{"disambiguationData":[OSD([sQuery(id+"F2.wireOp",EDGE,"E20")])]})});var subQ1=makeQuery(id+"F7.opExtrude","SWEPT_FACE",FACE,{"disambiguationData":[OSD([sQuery(id+"F6.wireOp",EDGE,"E25")])]});Q0=makeQuery(id+"FsIjI8eOMBiLZLS_1.boolean.opBoolean","SPLIT",EDGE,{"disambiguationData":[TD([makeQuery(id+"FsIjI8eOMBiLZLS_1.opExtrude","SWEPT_FACE",FACE,{"disambiguationData":[OSD([sQuery(id+"FMcGXzRqZ0D36rj_1.wireOp",EDGE,"461c5a9c-3a90-4efc-ba79-2a254029f436.top")])]})])],"derivedFrom":makeQuery(id+"F7.boolean.opBoolean","INTERSECT",EDGE,{"derivedFrom":[subQ0,subQ1]})});}
            var Q1;
            {var subQ0=makeQuery(id+"F3.boolean.opBoolean","COPY",FACE,{"derivedFrom":makeQuery(id+"F3.opExtrude","SWEPT_FACE",FACE,{"disambiguationData":[OSD([sQuery(id+"F2.wireOp",EDGE,"E20")])]})});var subQ1=makeQuery(id+"F7.opExtrude","SWEPT_FACE",FACE,{"disambiguationData":[OSD([sQuery(id+"F6.wireOp",EDGE,"E25")])]});Q1=makeQuery(id+"FsIjI8eOMBiLZLS_1.boolean.opBoolean","SPLIT",EDGE,{"disambiguationData":[TD([makeQuery(id+"FsIjI8eOMBiLZLS_1.opExtrude","SWEPT_FACE",FACE,{"disambiguationData":[OSD([sQuery(id+"FMcGXzRqZ0D36rj_1.wireOp",EDGE,"8841f1b6-027c-4d3d-bdc0-e0cde784121f.right")])]})])],"derivedFrom":makeQuery(id+"F7.boolean.opBoolean","INTERSECT",EDGE,{"derivedFrom":[subQ0,subQ1]})});}
            var Q2;
            {var subQ0=makeQuery(id+"F3.boolean.opBoolean","COPY",FACE,{"derivedFrom":makeQuery(id+"F3.opExtrude","SWEPT_FACE",FACE,{"disambiguationData":[OSD([sQuery(id+"F2.wireOp",EDGE,"E20")])]})});var subQ1=makeQuery(id+"F7.opExtrude","SWEPT_FACE",FACE,{"disambiguationData":[OSD([sQuery(id+"F6.wireOp",EDGE,"E25")])]});Q2=makeQuery(id+"FsIjI8eOMBiLZLS_1.boolean.opBoolean","SPLIT",EDGE,{"disambiguationData":[TD([makeQuery(id+"FsIjI8eOMBiLZLS_1.opExtrude","SWEPT_FACE",FACE,{"disambiguationData":[OSD([sQuery(id+"FMcGXzRqZ0D36rj_1.wireOp",EDGE,"8841f1b6-027c-4d3d-bdc0-e0cde784121f.top")])]})])],"derivedFrom":makeQuery(id+"F7.boolean.opBoolean","INTERSECT",EDGE,{"derivedFrom":[subQ0,subQ1]})});}
            var Q3;
            {var subQ0=makeQuery(id+"F3.boolean.opBoolean","COPY",FACE,{"derivedFrom":makeQuery(id+"F3.opExtrude","SWEPT_FACE",FACE,{"disambiguationData":[OSD([sQuery(id+"F2.wireOp",EDGE,"E20")])]})});var subQ1=makeQuery(id+"F7.opExtrude","SWEPT_FACE",FACE,{"disambiguationData":[OSD([sQuery(id+"F6.wireOp",EDGE,"E25")])]});Q3=makeQuery(id+"FsIjI8eOMBiLZLS_1.boolean.opBoolean","SPLIT",EDGE,{"disambiguationData":[TD([makeQuery(id+"FsIjI8eOMBiLZLS_1.opExtrude","SWEPT_FACE",FACE,{"disambiguationData":[OSD([sQuery(id+"FMcGXzRqZ0D36rj_1.wireOp",EDGE,"03bb9419-8f65-4d53-88c9-7e433d3c455f7.MirrorCS")])]})])],"derivedFrom":makeQuery(id+"F7.boolean.opBoolean","INTERSECT",EDGE,{"derivedFrom":[subQ0,subQ1]})});}
            var Q4;
            {var subQ0=makeQuery(id+"F3.boolean.opBoolean","COPY",FACE,{"derivedFrom":makeQuery(id+"F3.opExtrude","SWEPT_FACE",FACE,{"disambiguationData":[OSD([sQuery(id+"F2.wireOp",EDGE,"E20")])]})});var subQ1=makeQuery(id+"F7.opExtrude","SWEPT_FACE",FACE,{"disambiguationData":[OSD([sQuery(id+"F6.wireOp",EDGE,"E25")])]});Q4=makeQuery(id+"FsIjI8eOMBiLZLS_1.boolean.opBoolean","SPLIT",EDGE,{"disambiguationData":[TD([makeQuery(id+"FsIjI8eOMBiLZLS_1.opExtrude","SWEPT_FACE",FACE,{"disambiguationData":[OSD([sQuery(id+"FMcGXzRqZ0D36rj_1.wireOp",EDGE,"03bb9419-8f65-4d53-88c9-7e433d3c455f3.MirrorCS")])]})])],"derivedFrom":makeQuery(id+"F7.boolean.opBoolean","INTERSECT",EDGE,{"derivedFrom":[subQ0,subQ1]})});}
            var Q5;
            Q5=makeQuery(id+"F7.boolean.opBoolean","INTERSECT",EDGE,{"derivedFrom":[makeQuery(id+"F3.boolean.opBoolean","COPY",FACE,{"derivedFrom":makeQuery(id+"F3.opExtrude","SWEPT_FACE",FACE,{"disambiguationData":[OSD([sQuery(id+"F2.wireOp",EDGE,"E20")])]})}),makeQuery(id+"F7.opExtrude","SWEPT_FACE",FACE,{"disambiguationData":[OSD([sQuery(id+"F6.wireOp",EDGE,"E24.5")])]})]});
            var Q6;
            Q6=makeQuery(id+"F7.boolean.opBoolean","INTERSECT",EDGE,{"derivedFrom":[makeQuery(id+"F3.boolean.opBoolean","COPY",FACE,{"derivedFrom":makeQuery(id+"F3.opExtrude","SWEPT_FACE",FACE,{"disambiguationData":[OSD([sQuery(id+"F2.wireOp",EDGE,"E20")])]})}),makeQuery(id+"F7.opExtrude","SWEPT_FACE",FACE,{"disambiguationData":[OSD([sQuery(id+"F6.wireOp",EDGE,"E24.4")])]})]});
            var Q7;
            Q7=makeQuery(id+"F7.boolean.opBoolean","INTERSECT",EDGE,{"derivedFrom":[makeQuery(id+"F3.boolean.opBoolean","COPY",FACE,{"derivedFrom":makeQuery(id+"F3.opExtrude","SWEPT_FACE",FACE,{"disambiguationData":[OSD([sQuery(id+"F2.wireOp",EDGE,"E20")])]})}),makeQuery(id+"F7.opExtrude","SWEPT_FACE",FACE,{"disambiguationData":[OSD([sQuery(id+"F6.wireOp",EDGE,"E24.3")])]})]});
            var Q8;
            Q8=makeQuery(id+"F7.boolean.opBoolean","INTERSECT",EDGE,{"derivedFrom":[makeQuery(id+"F3.boolean.opBoolean","COPY",FACE,{"derivedFrom":makeQuery(id+"F3.opExtrude","SWEPT_FACE",FACE,{"disambiguationData":[OSD([sQuery(id+"F2.wireOp",EDGE,"E20")])]})}),makeQuery(id+"F7.opExtrude","SWEPT_FACE",FACE,{"disambiguationData":[OSD([sQuery(id+"F6.wireOp",EDGE,"E24.2")])]})]});
            var Q9;
            Q9=makeQuery(id+"F7.boolean.opBoolean","INTERSECT",EDGE,{"derivedFrom":[makeQuery(id+"F3.boolean.opBoolean","COPY",FACE,{"derivedFrom":makeQuery(id+"F3.opExtrude","SWEPT_FACE",FACE,{"disambiguationData":[OSD([sQuery(id+"F2.wireOp",EDGE,"E20")])]})}),makeQuery(id+"F7.opExtrude","SWEPT_FACE",FACE,{"disambiguationData":[OSD([sQuery(id+"F6.wireOp",EDGE,"E24.1")])]})]});
            var Q10;
            Q10=makeQuery(id+"F7.boolean.opBoolean","INTERSECT",EDGE,{"derivedFrom":[makeQuery(id+"F3.boolean.opBoolean","COPY",FACE,{"derivedFrom":makeQuery(id+"F3.opExtrude","SWEPT_FACE",FACE,{"disambiguationData":[OSD([sQuery(id+"F2.wireOp",EDGE,"E20")])]})}),makeQuery(id+"F7.opExtrude","SWEPT_FACE",FACE,{"disambiguationData":[OSD([sQuery(id+"F6.wireOp",EDGE,"E24.0")])]})]});
            var Q11;
            Q11=makeQuery(id+"F7.boolean.opBoolean","INTERSECT",EDGE,{"derivedFrom":[makeQuery(id+"F3.boolean.opBoolean","COPY",FACE,{"derivedFrom":makeQuery(id+"F3.opExtrude","SWEPT_FACE",FACE,{"disambiguationData":[OSD([sQuery(id+"F2.wireOp",EDGE,"E20")])]})}),makeQuery(id+"F7.opExtrude","SWEPT_FACE",FACE,{"disambiguationData":[OSD([sQuery(id+"F6.wireOp",EDGE,"E23.0")])]})]});
            var Q12;
            Q12=makeQuery(id+"F7.boolean.opBoolean","INTERSECT",EDGE,{"derivedFrom":[makeQuery(id+"F3.boolean.opBoolean","COPY",FACE,{"derivedFrom":makeQuery(id+"F3.opExtrude","SWEPT_FACE",FACE,{"disambiguationData":[OSD([sQuery(id+"F2.wireOp",EDGE,"E20")])]})}),makeQuery(id+"F7.opExtrude","SWEPT_FACE",FACE,{"disambiguationData":[OSD([sQuery(id+"F6.wireOp",EDGE,"E23.5")])]})]});
            var Q13;
            Q13=makeQuery(id+"F7.boolean.opBoolean","INTERSECT",EDGE,{"derivedFrom":[makeQuery(id+"F3.boolean.opBoolean","COPY",FACE,{"derivedFrom":makeQuery(id+"F3.opExtrude","SWEPT_FACE",FACE,{"disambiguationData":[OSD([sQuery(id+"F2.wireOp",EDGE,"E20")])]})}),makeQuery(id+"F7.opExtrude","SWEPT_FACE",FACE,{"disambiguationData":[OSD([sQuery(id+"F6.wireOp",EDGE,"E23.4")])]})]});
            var Q14;
            Q14=makeQuery(id+"F7.boolean.opBoolean","INTERSECT",EDGE,{"derivedFrom":[makeQuery(id+"F3.boolean.opBoolean","COPY",FACE,{"derivedFrom":makeQuery(id+"F3.opExtrude","SWEPT_FACE",FACE,{"disambiguationData":[OSD([sQuery(id+"F2.wireOp",EDGE,"E20")])]})}),makeQuery(id+"F7.opExtrude","SWEPT_FACE",FACE,{"disambiguationData":[OSD([sQuery(id+"F6.wireOp",EDGE,"E23.3")])]})]});
            var Q15;
            Q15=makeQuery(id+"F7.boolean.opBoolean","INTERSECT",EDGE,{"derivedFrom":[makeQuery(id+"F3.boolean.opBoolean","COPY",FACE,{"derivedFrom":makeQuery(id+"F3.opExtrude","SWEPT_FACE",FACE,{"disambiguationData":[OSD([sQuery(id+"F2.wireOp",EDGE,"E20")])]})}),makeQuery(id+"F7.opExtrude","SWEPT_FACE",FACE,{"disambiguationData":[OSD([sQuery(id+"F6.wireOp",EDGE,"E23.2")])]})]});
            var Q16;
            Q16=makeQuery(id+"F7.boolean.opBoolean","INTERSECT",EDGE,{"derivedFrom":[makeQuery(id+"F3.boolean.opBoolean","COPY",FACE,{"derivedFrom":makeQuery(id+"F3.opExtrude","SWEPT_FACE",FACE,{"disambiguationData":[OSD([sQuery(id+"F2.wireOp",EDGE,"E20")])]})}),makeQuery(id+"F7.opExtrude","SWEPT_FACE",FACE,{"disambiguationData":[OSD([sQuery(id+"F6.wireOp",EDGE,"E23.1")])]})]});
            var Q17;
            {var subQ0=makeQuery(id+"F3.boolean.opBoolean","COPY",FACE,{"derivedFrom":makeQuery(id+"F3.opExtrude","SWEPT_FACE",FACE,{"disambiguationData":[OSD([sQuery(id+"F2.wireOp",EDGE,"E20")])]})});var subQ1=makeQuery(id+"F7.opExtrude","SWEPT_FACE",FACE,{"disambiguationData":[OSD([sQuery(id+"F6.wireOp",EDGE,"E26")])]});Q17=makeQuery(id+"FsIjI8eOMBiLZLS_1.boolean.opBoolean","SPLIT",EDGE,{"disambiguationData":[TD([makeQuery(id+"FsIjI8eOMBiLZLS_1.opExtrude","SWEPT_FACE",FACE,{"disambiguationData":[OSD([sQuery(id+"FMcGXzRqZ0D36rj_1.wireOp",EDGE,"a05d47f6-6ef9-45c5-bd43-407b3eb50070.top")])]})])],"derivedFrom":makeQuery(id+"F7.boolean.opBoolean","INTERSECT",EDGE,{"derivedFrom":[subQ0,subQ1]})});}
            var Q18;
            {var subQ0=makeQuery(id+"F3.boolean.opBoolean","COPY",FACE,{"derivedFrom":makeQuery(id+"F3.opExtrude","SWEPT_FACE",FACE,{"disambiguationData":[OSD([sQuery(id+"F2.wireOp",EDGE,"E20")])]})});var subQ1=makeQuery(id+"F7.opExtrude","SWEPT_FACE",FACE,{"disambiguationData":[OSD([sQuery(id+"F6.wireOp",EDGE,"E26")])]});Q18=makeQuery(id+"FsIjI8eOMBiLZLS_1.boolean.opBoolean","SPLIT",EDGE,{"disambiguationData":[TD([makeQuery(id+"FsIjI8eOMBiLZLS_1.opExtrude","SWEPT_FACE",FACE,{"disambiguationData":[OSD([sQuery(id+"FMcGXzRqZ0D36rj_1.wireOp",EDGE,"40be6d43-4c42-4233-b96d-31cddbe2ae95.right")])]})])],"derivedFrom":makeQuery(id+"F7.boolean.opBoolean","INTERSECT",EDGE,{"derivedFrom":[subQ0,subQ1]})});}
            var Q19;
            {var subQ0=makeQuery(id+"F3.boolean.opBoolean","COPY",FACE,{"derivedFrom":makeQuery(id+"F3.opExtrude","SWEPT_FACE",FACE,{"disambiguationData":[OSD([sQuery(id+"F2.wireOp",EDGE,"E20")])]})});var subQ1=makeQuery(id+"F7.opExtrude","SWEPT_FACE",FACE,{"disambiguationData":[OSD([sQuery(id+"F6.wireOp",EDGE,"E26")])]});Q19=makeQuery(id+"FsIjI8eOMBiLZLS_1.boolean.opBoolean","SPLIT",EDGE,{"disambiguationData":[TD([makeQuery(id+"FsIjI8eOMBiLZLS_1.opExtrude","SWEPT_FACE",FACE,{"disambiguationData":[OSD([sQuery(id+"FMcGXzRqZ0D36rj_1.wireOp",EDGE,"40be6d43-4c42-4233-b96d-31cddbe2ae95.top")])]})])],"derivedFrom":makeQuery(id+"F7.boolean.opBoolean","INTERSECT",EDGE,{"derivedFrom":[subQ0,subQ1]})});}
            var Q20;
            {var subQ0=makeQuery(id+"F3.boolean.opBoolean","COPY",FACE,{"derivedFrom":makeQuery(id+"F3.opExtrude","SWEPT_FACE",FACE,{"disambiguationData":[OSD([sQuery(id+"F2.wireOp",EDGE,"E20")])]})});var subQ1=makeQuery(id+"F7.opExtrude","SWEPT_FACE",FACE,{"disambiguationData":[OSD([sQuery(id+"F6.wireOp",EDGE,"E26")])]});Q20=makeQuery(id+"FsIjI8eOMBiLZLS_1.boolean.opBoolean","SPLIT",EDGE,{"disambiguationData":[TD([makeQuery(id+"FsIjI8eOMBiLZLS_1.opExtrude","SWEPT_FACE",FACE,{"disambiguationData":[OSD([sQuery(id+"FMcGXzRqZ0D36rj_1.wireOp",EDGE,"03bb9419-8f65-4d53-88c9-7e433d3c455f27.MirrorCS")])]})])],"derivedFrom":makeQuery(id+"F7.boolean.opBoolean","INTERSECT",EDGE,{"derivedFrom":[subQ0,subQ1]})});}
            fillet(context, id + "F23", {"entities" : qUnion([Q0, Q1, Q2, Q3, Q4, Q5, Q6, Q7, Q8, Q9, Q10, Q11, Q12, Q13, Q14, Q15, Q16, Q17, Q18, Q19, Q20]), "radius" : 0.3 * mm, "allowEdgeOverflow" : false});
        }
    });
